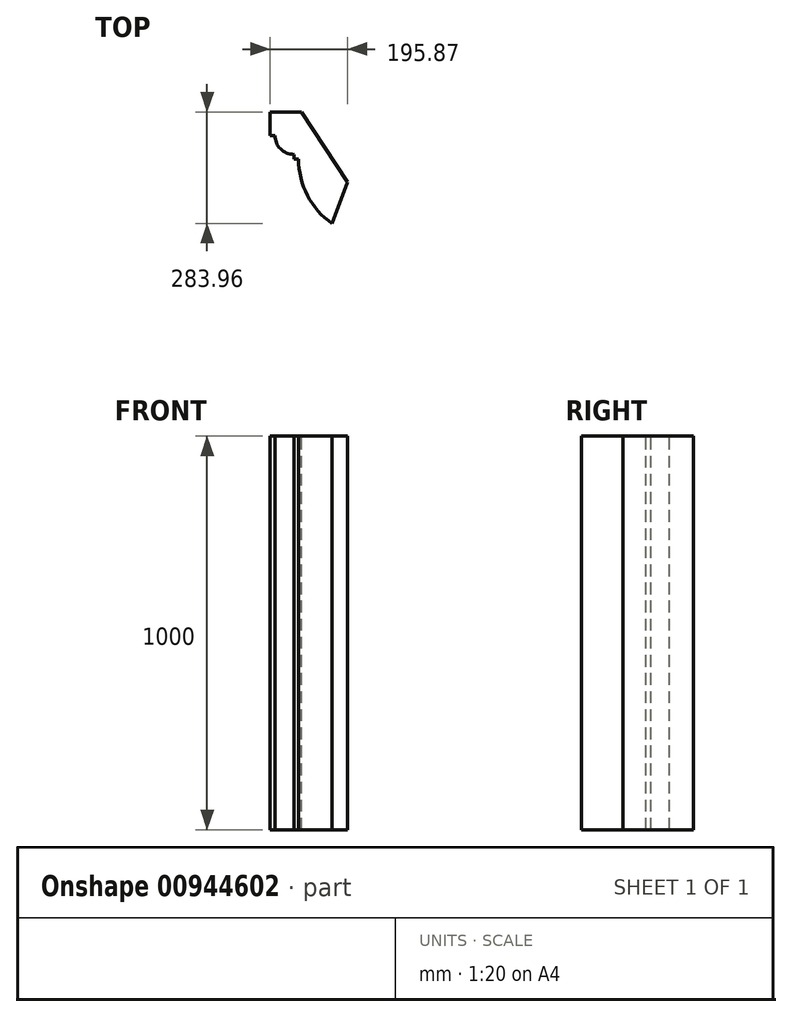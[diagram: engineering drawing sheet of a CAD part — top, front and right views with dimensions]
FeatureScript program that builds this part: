
annotation { "Feature Type Name" : "Feature", "Feature Type Description" : "" }
export const myFeature = defineFeature(function(context is Context, id is Id, definition is map)
    precondition{}
    {
        {
            var Q0;
            Q0=qCreatedBy(makeId("Top.planeOp"),FACE);
            var sketch = newSketch(context, id + "F0", { "sketchPlane" : qUnion([Q0])});
            skLineSegment(sketch, "E0", {"start": v(0, 0) * mm, "end": v(-115.87, 178.12) * mm});
            skLineSegment(sketch, "E1", {"start": v(-115.87, 178.12) * mm, "end": v(-195.87, 178.12) * mm});
            skLineSegment(sketch, "E2", {"start": v(-195.87, 178.12) * mm, "end": v(-195.87, 118.12) * mm});
            skLineSegment(sketch, "E3", {"start": v(-195.87, 118.12) * mm, "end": v(-183.87, 118.12) * mm});
            skLineSegment(sketch, "E4", {"start": v(0, 0) * mm, "end": v(-38.4, -105.84) * mm});
            skLineSegment(sketch, "E5", {"start": v(-183.87, 118.12) * mm, "end": v(-135.87, 118.12) * mm, "construction": true});
            skArc(sketch, "E6", {"start": v(-183.87, 118.12) * mm, "mid": v(-169.82, 84.18) * mm, "end": v(-135.87, 70.12) * mm});
            skLineSegment(sketch, "E7", {"start": v(-135.87, 70.12) * mm, "end": v(-135.87, 58.12) * mm});
            skLineSegment(sketch, "E8", {"start": v(-135.87, 58.12) * mm, "end": v(-123.87, 58.12) * mm});
            skLineSegment(sketch, "E9", {"start": v(-123.87, 58.12) * mm, "end": v(76.13, 58.12) * mm, "construction": true});
            skArc(sketch, "E10", {"start": v(-123.87, 58.12) * mm, "mid": v(-101.22, -34.33) * mm, "end": v(-38.4, -105.84) * mm});
            skLineSegment(sketch, "E11", {"start": v(76.13, 58.12) * mm, "end": v(7.92, -129.89) * mm, "construction": true});
            skSolve(sketch);
        }
        {
            var Q0;
            Q0=qCreatedBy(makeId("Front.planeOp"),FACE);
            var Q1;
            Q1=sQuery(id+"F0.wireOp",VERTEX,"E4.end");
            cPlane(context, id + "F1", {"entities" : qUnion([Q0, Q1]), "cplaneType" : CPlaneType.PLANE_POINT, "offset" : 104 * mm, "width" : 150 * mm, "height" : 150 * mm});
        }
        {
            var Q0;
            Q0=qCreatedBy(id+"F1.planeOp",FACE);
            var sketch = newSketch(context, id + "F2", { "sketchPlane" : qUnion([Q0])});
            skPoint(sketch, "E12.0", {"position": v(-38.4, 0) * mm});
            skLineSegment(sketch, "E13", {"start": v(-38.4, 0) * mm, "end": v(961.6, 0) * mm, "construction": true});
            skLineSegment(sketch, "E14", {"start": v(961.6, 0) * mm, "end": v(961.6, 1000) * mm, "construction": true});
            skLineSegment(sketch, "E15", {"start": v(-38.4, 0) * mm, "end": v(-38.4, 1000) * mm});
            skSolve(sketch);
        }
        {
            var Q0;
            Q0=qSketchRegion(id+"F0",true);
            var Q1;
            Q1=qConstructionFilter(qBodyType(qCreatedBy(id+"F2",EDGE),BodyType.WIRE),ConstructionObject.NO);
            sweep(context, id + "F3", {"profiles" : qUnion([Q0]), "path" : qUnion([Q1])});
        }
    });
